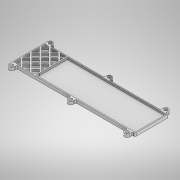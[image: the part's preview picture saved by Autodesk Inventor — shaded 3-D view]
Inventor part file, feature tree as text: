
AUTODESK INVENTOR PART (.ipt)
format: ipt  version: 2021 (Build 250183000, 183)  size: 536,064 bytes
history: native  units: mm
features: extrude x4, sketch x4, projected_geometry x2, fillet x1
ambient origin geometry x8: Origin, YZ Plane, XZ Plane, XY Plane, X Axis, Y Axis, Z Axis, Center Point
bodies: Solid1 (feature_tree)
feature tree (11):
  extrude  "Extrusion1"  Depth=30.0mm
  extrude  "Extrusion2"  Depth=1.0mm
  fillet  "Fillet2"  Radius=1.0mm
  extrude  "Extrusion5"  Depth=17.5mm
  extrude  "Extrusion16"  Depth=1.0mm
  sketch  "Sketch1"  dims[d0=37.0mm d1=30.0mm]
  sketch  "Sketch2"  dims[d2=18.0mm d3=37.5mm d4=1.0mm]
  projected_geometry  "Projected Loop1"
  sketch  "Sketch5"  dims[d5=6.0mm d6=17.5mm]
  sketch  "Sketch14"  dims[d7=28.0mm d8=1.0mm d9=1.0mm d10=1.0mm d11=1.0mm d12=117.5mm d13=2.0mm d14=2.0mm d15=1.0mm d16=1.0mm d17=2.0mm d18=2.0mm d19=2.0mm d20=2.0mm d21=2.5mm d22=2.5mm d23=5.0mm d24=2.5mm d25=2.5mm d26=2.5mm d27=2.5mm d28=5.0mm d29=5.0mm d30=2.5mm d31=3.1mm d32=3.1mm d33=3.1mm d34=3.1mm d35=3.1mm d36=3.1mm d37=7.0mm d38=0.0mm d39=1.0mm d40=0.0mm d44=1.0mm d45=1.0mm d46=0.5mm d47=0.0mm d48=1.0mm d49=1.0mm d50=1.0mm d51=1.0mm d53=1.0mm d61=7.0mm d62=0.0mm d127=1.0mm d128=1.0mm d129=1.0mm d130=22.5mm d131=2.0mm d132=0.0mm d133=1.0mm d134=1.0mm d135=1.0mm d136=5.0mm d137=5.0mm d138=0.0mm d139=0.0mm d140=5.0mm d141=5.0mm d142=30.0mm d144=9.0mm d145=40.0mm d147=9.0mm]
  projected_geometry  "Projected Loop4"
